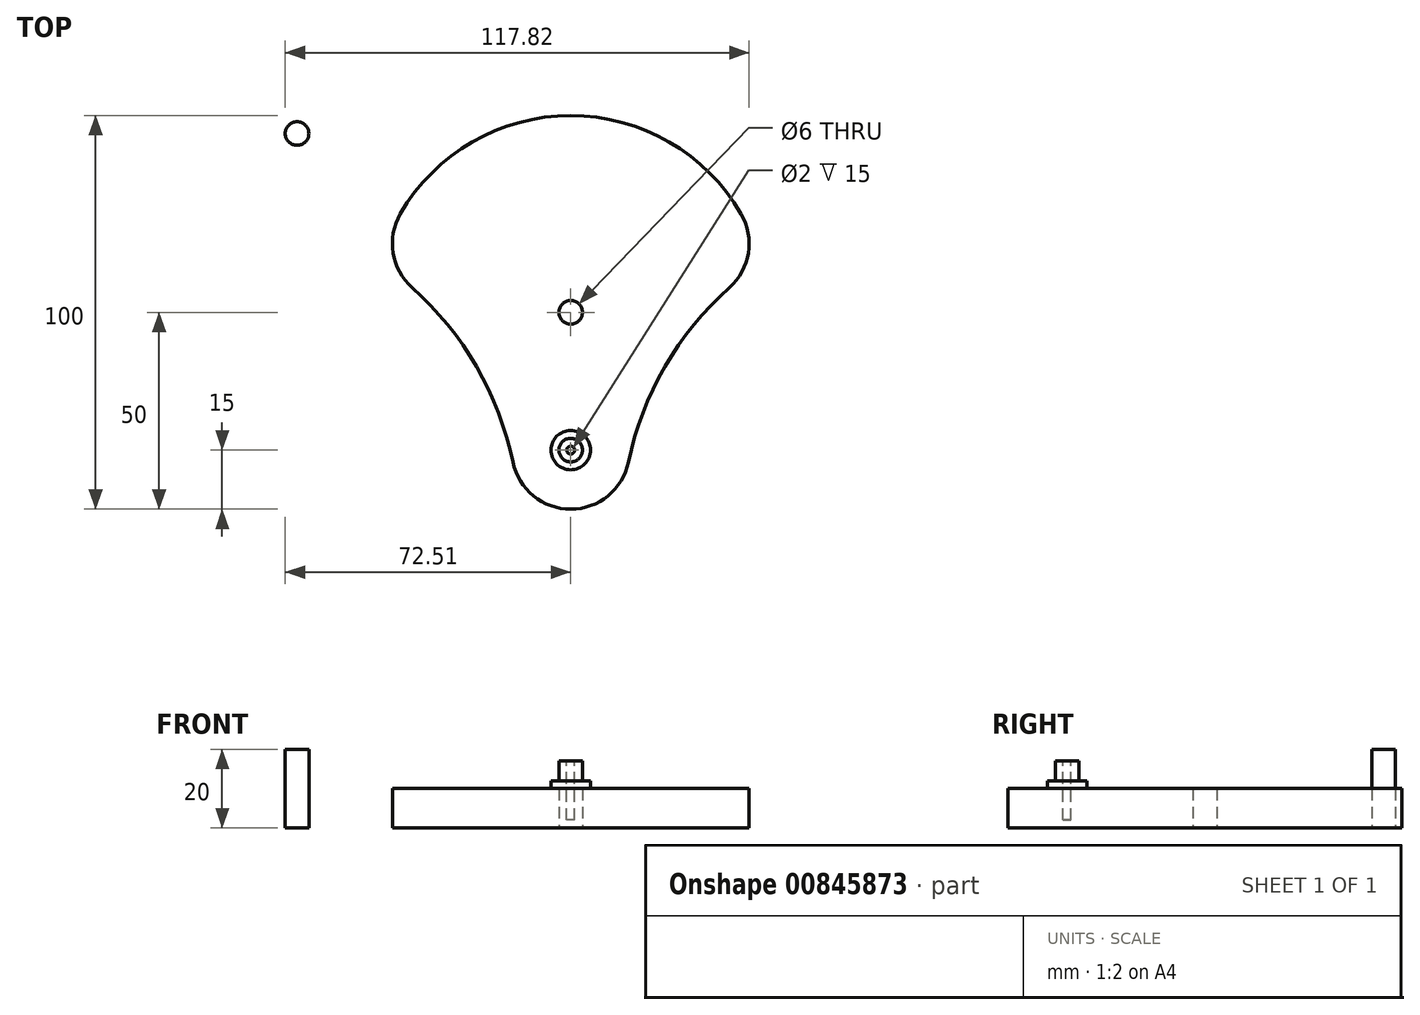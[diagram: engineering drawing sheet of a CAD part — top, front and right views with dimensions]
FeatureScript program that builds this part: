
annotation { "Feature Type Name" : "Feature", "Feature Type Description" : "" }
export const myFeature = defineFeature(function(context is Context, id is Id, definition is map)
    precondition{}
    {
        {
            var Q0;
            Q0=qCreatedBy(makeId("Top.planeOp"),FACE);
            var sketch = newSketch(context, id + "F0", { "sketchPlane" : qUnion([Q0])});
            skCircle(sketch, "E0", {"center": v(0, 0) * mm, "radius": 50 * mm});
            skCircle(sketch, "E1", {"center": v(0, 0) * mm, "radius": 3 * mm});
            skCircle(sketch, "E2", {"center": v(0, -35) * mm, "radius": 5 * mm});
            skCircle(sketch, "E3", {"center": v(0, -35) * mm, "radius": 15 * mm});
            skCircle(sketch, "E4.1.0", {"center": v(30.31, 17.5) * mm, "radius": 15 * mm});
            skCircle(sketch, "E4.2.0", {"center": v(-30.31, 17.5) * mm, "radius": 15 * mm});
            skArc(sketch, "E5", {"start": v(40.3, 6.3) * mm, "mid": v(23.92, -13.81) * mm, "end": v(14.69, -38.04) * mm});
            skArc(sketch, "E6.2.0", {"start": v(-14.69, -38.04) * mm, "mid": v(-23.92, -13.81) * mm, "end": v(-40.3, 6.3) * mm});
            skCircle(sketch, "E7", {"center": v(0, -35) * mm, "radius": 3 * mm});
            skCircle(sketch, "E8", {"center": v(-69.51, 45.44) * mm, "radius": 3 * mm});
            skSolve(sketch);
        }
        {
            var Q0;
            Q0=makeQuery(id+"F0.imprint","IMPRINT",FACE,{"disambiguationData":[TD([[makeQuery(id+"F0.imprint","IMPRINT",EDGE,{"derivedFrom":sQuery(id+"F0.wireOp",EDGE,"E1")}),-1.0]])]});
            var Q1;
            {var subQ0=sQuery(id+"F0.wireOp",EDGE,"E4.2.0");var subQ1=makeQuery(id+"F0.imprint","INTERSECT",VERTEX,{"derivedFrom":[subQ0,sQuery(id+"F0.wireOp",EDGE,"E6.2.0")]});Q1=makeQuery(id+"F0.imprint","IMPRINT",FACE,{"disambiguationData":[TD([[makeQuery(id+"F0.imprint","IMPRINT",EDGE,{"disambiguationData":[TD([[subQ1,1.0]])],"derivedFrom":subQ0}),1.0]])]});}
            var Q2;
            {var subQ0=sQuery(id+"F0.wireOp",EDGE,"E4.1.0");var subQ1=makeQuery(id+"F0.imprint","INTERSECT",VERTEX,{"derivedFrom":[subQ0,sQuery(id+"F0.wireOp",EDGE,"E5")]});Q2=makeQuery(id+"F0.imprint","IMPRINT",FACE,{"disambiguationData":[TD([[makeQuery(id+"F0.imprint","IMPRINT",EDGE,{"disambiguationData":[TD([[subQ1,-1.0]])],"derivedFrom":subQ0}),1.0]])]});}
            var Q3;
            Q3=makeQuery(id+"F0.imprint","IMPRINT",FACE,{"disambiguationData":[TD([[makeQuery(id+"F0.imprint","IMPRINT",EDGE,{"derivedFrom":sQuery(id+"F0.wireOp",EDGE,"E2")}),-1.0]])]});
            extrude(context, id + "F1", {"entities" : qUnion([Q0, Q1, Q2, Q3]), "depth" : 10 * mm, "offsetDistance" : 25 * mm});
        }
        {
            var Q0;
            Q0=makeQuery(id+"F0.imprint","IMPRINT",FACE,{"disambiguationData":[TD([[makeQuery(id+"F0.imprint","IMPRINT",EDGE,{"derivedFrom":sQuery(id+"F0.wireOp",EDGE,"E2")}),1.0]])]});
            extrude(context, id + "F2", {"entities" : qUnion([Q0]), "operationType" : NewBodyOperationType.ADD, "depth" : 12 * mm, "offsetDistance" : 25 * mm});
        }
        {
            var Q0;
            Q0=makeQuery(id+"F0.imprint","IMPRINT",FACE,{"disambiguationData":[TD([[makeQuery(id+"F0.imprint","IMPRINT",EDGE,{"derivedFrom":sQuery(id+"F0.wireOp",EDGE,"E7")}),1.0]])]});
            extrude(context, id + "F3", {"entities" : qUnion([Q0]), "operationType" : NewBodyOperationType.ADD, "depth" : 17 * mm, "offsetDistance" : 25 * mm});
        }
        {
            var Q0;
            Q0=makeQuery(id+"F3.opExtrude","CAP_FACE",FACE,{"disambiguationData":[OSD([sQuery(id+"F0.wireOp",EDGE,"E7")])],"isStart":false});
            var sketch = newSketch(context, id + "F4", { "sketchPlane" : qUnion([Q0])});
            skCircle(sketch, "E9", {"center": v(0, -35) * mm, "radius": 1 * mm});
            skSolve(sketch);
        }
        {
            var Q0;
            Q0=makeQuery(id+"F4.imprint","IMPRINT",FACE,{"disambiguationData":[TD([[makeQuery(id+"F4.imprint","IMPRINT",EDGE,{"derivedFrom":sQuery(id+"F4.wireOp",EDGE,"E9")}),1.0]])]});
            extrude(context, id + "F5", {"entities" : qUnion([Q0]), "operationType" : NewBodyOperationType.REMOVE, "oppositeDirection" : true, "depth" : 15 * mm, "offsetDistance" : 25 * mm});
        }
        {
            var Q0;
            Q0=makeQuery(id+"F0.imprint","IMPRINT",FACE,{"disambiguationData":[TD([[makeQuery(id+"F0.imprint","IMPRINT",EDGE,{"derivedFrom":sQuery(id+"F0.wireOp",EDGE,"E8")}),1.0]])]});
            extrude(context, id + "F6", {"entities" : qUnion([Q0]), "depth" : 20 * mm, "offsetDistance" : 25 * mm});
        }
    });
